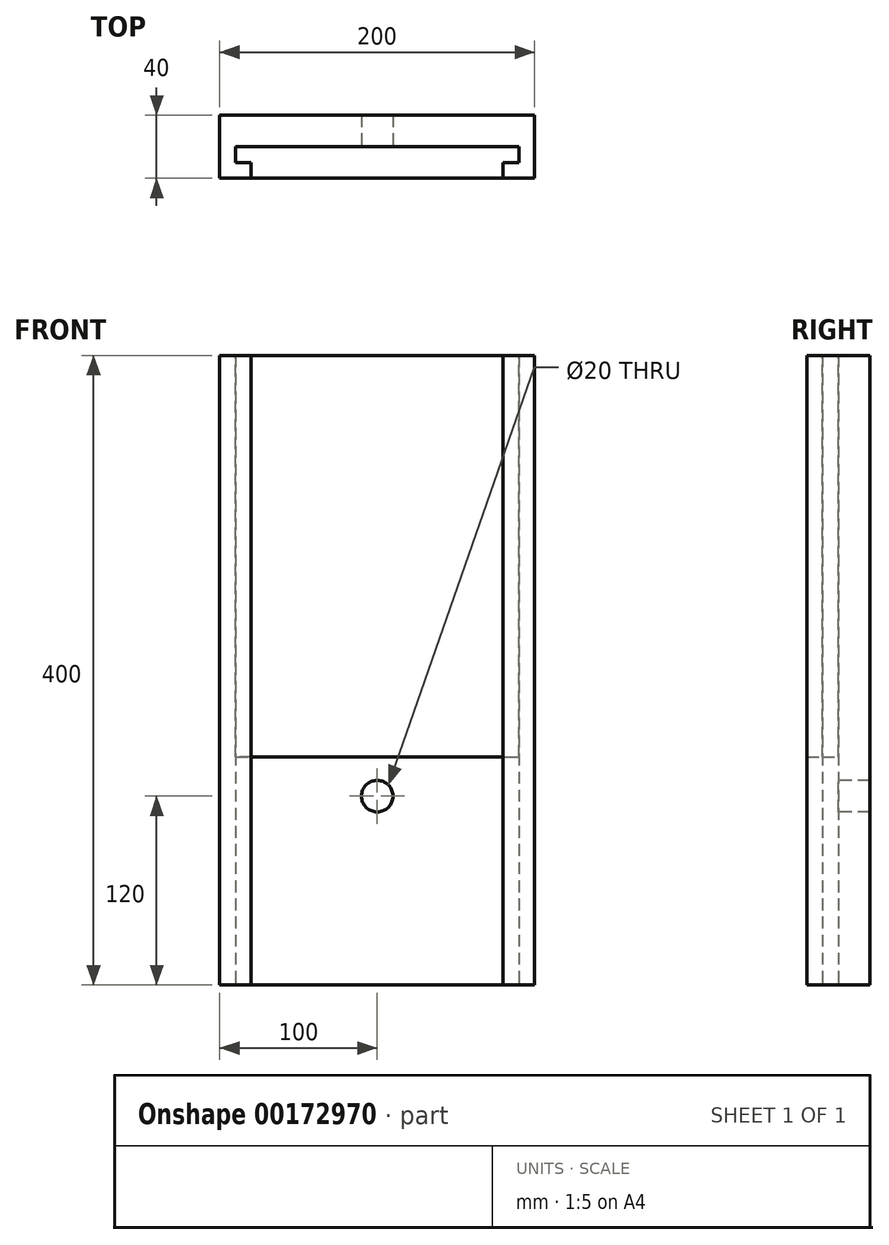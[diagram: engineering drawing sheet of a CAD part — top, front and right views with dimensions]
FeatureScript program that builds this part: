
annotation { "Feature Type Name" : "Feature", "Feature Type Description" : "" }
export const myFeature = defineFeature(function(context is Context, id is Id, definition is map)
    precondition{}
    {
        {
            var Q0;
            Q0=qCreatedBy(makeId("Top.planeOp"),FACE);
            var sketch = newSketch(context, id + "F0", { "sketchPlane" : qUnion([Q0])});
            skLineSegment(sketch, "E0", {"start": v(0, 40) * mm, "end": v(100, 40) * mm});
            skLineSegment(sketch, "E1", {"start": v(100, 40) * mm, "end": v(100, 0) * mm});
            skLineSegment(sketch, "E2", {"start": v(100, 0) * mm, "end": v(80, 0) * mm});
            skLineSegment(sketch, "E3", {"start": v(80, 0) * mm, "end": v(80, 10) * mm});
            skLineSegment(sketch, "E4", {"start": v(80, 10) * mm, "end": v(90, 10) * mm});
            skLineSegment(sketch, "E5", {"start": v(90, 10) * mm, "end": v(90, 20) * mm});
            skLineSegment(sketch, "E6", {"start": v(90, 20) * mm, "end": v(0, 20) * mm});
            skLineSegment(sketch, "E7", {"start": v(0, 40) * mm, "end": v(0, 0) * mm, "construction": true});
            skLineSegment(sketch, "E8.MirrorCS", {"start": v(-90, 20) * mm, "end": v(0, 20) * mm});
            skLineSegment(sketch, "E9.MirrorCS", {"start": v(0, 40) * mm, "end": v(-100, 40) * mm});
            skLineSegment(sketch, "E10.MirrorCS", {"start": v(-90, 10) * mm, "end": v(-90, 20) * mm});
            skLineSegment(sketch, "E11.MirrorCS", {"start": v(-80, 10) * mm, "end": v(-90, 10) * mm});
            skLineSegment(sketch, "E12.MirrorCS", {"start": v(-80, 0) * mm, "end": v(-80, 10) * mm});
            skLineSegment(sketch, "E13.MirrorCS", {"start": v(-100, 0) * mm, "end": v(-80, 0) * mm});
            skLineSegment(sketch, "E14.MirrorCS", {"start": v(-100, 40) * mm, "end": v(-100, 0) * mm});
            skSolve(sketch);
        }
        {
            var Q0;
            Q0 = qSketchRegion(id + "F0", true);
            var Q1;
            Q1=makeQuery(id+"F0.imprint","IMPRINT",FACE,{"disambiguationData":[TD([[makeQuery(id+"F0.imprint","IMPRINT",EDGE,{"derivedFrom":sQuery(id+"F0.wireOp",EDGE,"E0")}),-1.0]])]});
            extrude(context, id + "F1", {"entities" : qUnion([Q0, Q1]), "depth" : 280 * mm, "hasSecondDirection" : true, "secondDirectionOppositeDirection" : true, "secondDirectionDepth" : 120 * mm});
        }
        {
            var Q0;
            Q0=makeQuery(id+"F1.opExtrude","SWEPT_FACE",FACE,{"disambiguationData":[OSD([sQuery(id+"F0.wireOp",EDGE,"E6"),sQuery(id+"F0.wireOp",EDGE,"E8.MirrorCS")])]});
            var sketch = newSketch(context, id + "F2", { "sketchPlane" : qUnion([Q0])});
            skCircle(sketch, "E15", {"center": v(0, 0) * mm, "radius": 10 * mm});
            skSolve(sketch);
        }
        {
            var Q0;
            Q0 = qSketchRegion(id + "F2", true);
            extrude(context, id + "F3", {"entities" : qUnion([Q0]), "operationType" : NewBodyOperationType.REMOVE, "oppositeDirection" : true, "depth" : 20 * mm});
        }
        {
            var Q0;
            Q0=makeQuery(id+"F1.opExtrude","CAP_FACE",FACE,{"disambiguationData":[OSD([sQuery(id+"F0.wireOp",EDGE,"E0"),sQuery(id+"F0.wireOp",EDGE,"E1"),sQuery(id+"F0.wireOp",EDGE,"E2"),sQuery(id+"F0.wireOp",EDGE,"E3"),sQuery(id+"F0.wireOp",EDGE,"E4"),sQuery(id+"F0.wireOp",EDGE,"E5"),sQuery(id+"F0.wireOp",EDGE,"E6"),sQuery(id+"F0.wireOp",EDGE,"E8.MirrorCS"),sQuery(id+"F0.wireOp",EDGE,"E9.MirrorCS"),sQuery(id+"F0.wireOp",EDGE,"E10.MirrorCS"),sQuery(id+"F0.wireOp",EDGE,"E11.MirrorCS"),sQuery(id+"F0.wireOp",EDGE,"E12.MirrorCS"),sQuery(id+"F0.wireOp",EDGE,"E13.MirrorCS"),sQuery(id+"F0.wireOp",EDGE,"E14.MirrorCS")])],"isStart":false});
            var sketch = newSketch(context, id + "F4", { "sketchPlane" : qUnion([Q0])});
            skLineSegment(sketch, "E16", {"start": v(-80, 0) * mm, "end": v(-80, 10) * mm});
            skLineSegment(sketch, "E17", {"start": v(-80, 10) * mm, "end": v(-90, 10) * mm});
            skLineSegment(sketch, "E18", {"start": v(-90, 10) * mm, "end": v(-90, 20) * mm});
            skLineSegment(sketch, "E19", {"start": v(-90, 20) * mm, "end": v(90, 20) * mm});
            skLineSegment(sketch, "E20", {"start": v(90, 20) * mm, "end": v(90, 10) * mm});
            skLineSegment(sketch, "E21", {"start": v(90, 10) * mm, "end": v(80, 10) * mm});
            skLineSegment(sketch, "E22", {"start": v(80, 10) * mm, "end": v(80, 0) * mm});
            skLineSegment(sketch, "E23", {"start": v(80, 0) * mm, "end": v(-80, 0) * mm});
            skSolve(sketch);
        }
        {
            var Q0;
            Q0 = qSketchRegion(id + "F4", true);
            extrude(context, id + "F5", {"entities" : qUnion([Q0]), "oppositeDirection" : true, "depth" : 255 * mm});
        }
    });
